FCSTD DOCUMENT  (FreeCAD 0.21R33668 +26 (Git))
Label: MasterSketch
License: All rights reserved
LicenseURL: http://en.wikipedia.org/wiki/All_rights_reserved
objects: Sketcher::SketchObject×1, PartDesign::CoordinateSystem×1, PartDesign::Body×1
note: 3 computed .brp shape members not serialized (recipe doc carries the construction recipe); baked Part::Feature solids carry a one-line shape summary decoded from their .brp

FEATURE [Sketcher::SketchObject] Sketch
  FullyConstrained = true
  MapMode = 5
  Support = -> [XY_Plane]
  sketch-geometry (5):
    g0: LineSegment StartX=33.675 StartY=-26.83 StartZ=0 EndX=33.675 EndY=26.83 EndZ=0
    g1: LineSegment StartX=33.675 StartY=26.83 StartZ=0 EndX=-33.675 EndY=26.83 EndZ=0
    g2: LineSegment StartX=-33.675 StartY=26.83 StartZ=0 EndX=-33.675 EndY=-26.83 EndZ=0
    g3: LineSegment StartX=-33.675 StartY=-26.83 StartZ=0 EndX=33.675 EndY=-26.83 EndZ=0
    g4: GeomPoint X=0 Y=0 Z=0
  constraints (12):
    c: Coincident(g0,g1)
    c: Coincident(g1,g2)
    c: Coincident(g2,g3)
    c: Coincident(g3,g0)
    c: Horizontal(g1)
    c: Horizontal(g3)
    c: Vertical(g0)
    c: Vertical(g2)
    c: Symmetric(g1,g0,g4)
    c: Coincident(g4,g-1)
    c: DistanceX(g1,g1) = 67.35
    c: DistanceY(g0,g0) = 53.66
FEATURE [PartDesign::CoordinateSystem] Local_CS
  AttacherType = Attacher::AttachEngine3D
  MapMode = 2
  Support = -> [Sketch]
FEATURE [PartDesign::Body] Body
  Group = -> [Sketch,Local_CS]
  Origin = -> Origin
